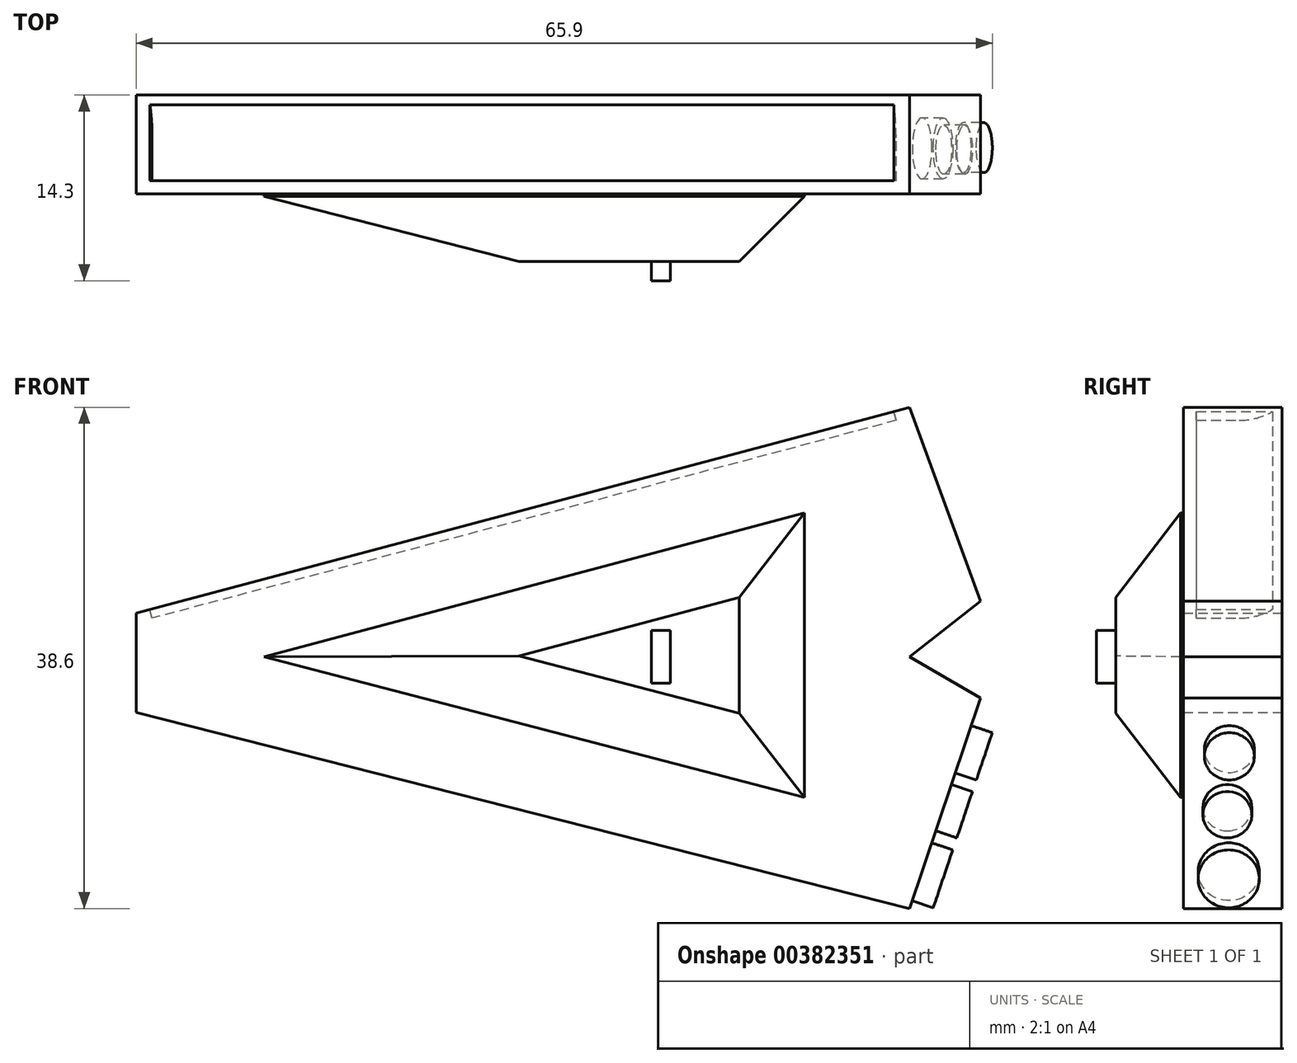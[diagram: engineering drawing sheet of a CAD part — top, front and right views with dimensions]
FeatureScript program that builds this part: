
annotation { "Feature Type Name" : "Feature", "Feature Type Description" : "" }
export const myFeature = defineFeature(function(context is Context, id is Id, definition is map)
    precondition{}
    {
        {
            var Q0;
            Q0=qCreatedBy(makeId("Front.planeOp"),FACE);
            var sketch = newSketch(context, id + "F0", { "sketchPlane" : qUnion([Q0])});
            skLineSegment(sketch, "E0", {"start": v(-59.54, 3.37) * mm, "end": v(-59.54, -4.28) * mm});
            skLineSegment(sketch, "E1", {"start": v(-59.54, -4.28) * mm, "end": v(0, -19.4) * mm});
            skLineSegment(sketch, "E2", {"start": v(0, -19.4) * mm, "end": v(5.46, -3.19) * mm});
            skLineSegment(sketch, "E3", {"start": v(5.46, -3.19) * mm, "end": v(0, 0) * mm});
            skLineSegment(sketch, "E4", {"start": v(0, 0) * mm, "end": v(5.46, 4.28) * mm});
            skLineSegment(sketch, "E5", {"start": v(5.46, 4.28) * mm, "end": v(0, 19.2) * mm});
            skLineSegment(sketch, "E6", {"start": v(0, 19.2) * mm, "end": v(-59.54, 3.37) * mm});
            skSolve(sketch);
        }
        {
            var Q0;
            Q0 = qSketchRegion(id + "F0", true);
            extrude(context, id + "F1", {"entities" : qUnion([Q0]), "depth" : 7.6 * mm});
        }
        {
            var Q0;
            Q0=makeQuery(id+"F1.opExtrude","CAP_FACE",FACE,{"disambiguationData":[OSD([sQuery(id+"F0.wireOp",EDGE,"E0"),sQuery(id+"F0.wireOp",EDGE,"E1"),sQuery(id+"F0.wireOp",EDGE,"E2"),sQuery(id+"F0.wireOp",EDGE,"E3"),sQuery(id+"F0.wireOp",EDGE,"E4"),sQuery(id+"F0.wireOp",EDGE,"E5"),sQuery(id+"F0.wireOp",EDGE,"E6")])],"isStart":false});
            var sketch = newSketch(context, id + "F2", { "sketchPlane" : qUnion([Q0])});
            skLineSegment(sketch, "E7", {"start": v(-49.7, 0) * mm, "end": v(-8.11, 11.07) * mm});
            skLineSegment(sketch, "E8", {"start": v(-8.11, 11.07) * mm, "end": v(-8.11, -10.83) * mm});
            skLineSegment(sketch, "E9", {"start": v(-8.11, -10.83) * mm, "end": v(-49.7, 0) * mm});
            skSolve(sketch);
        }
        {
            var Q0;
            Q0=makeQuery(id+"F2.imprint","IMPRINT",FACE,{"disambiguationData":[TD([[makeQuery(id+"F2.imprint","IMPRINT",EDGE,{"derivedFrom":sQuery(id+"F2.wireOp",EDGE,"E7")}),-1.0]])]});
            extrude(context, id + "F3", {"entities" : qUnion([Q0]), "operationType" : NewBodyOperationType.ADD, "depth" : 5.2 * mm});
        }
        {
            var Q0;
            Q0=makeQuery(id+"F1.opExtrude","SWEPT_FACE",FACE,{"disambiguationData":[OSD([sQuery(id+"F0.wireOp",EDGE,"E2")])]});
            var sketch = newSketch(context, id + "F4", { "sketchPlane" : qUnion([Q0])});
            skCircle(sketch, "E10", {"center": v(-4.2, -10.18) * mm, "radius": 1.88 * mm});
            skCircle(sketch, "E11", {"center": v(-4.05, -5.43) * mm, "radius": 1.92 * mm});
            skCircle(sketch, "E12", {"center": v(-4.1, -15.39) * mm, "radius": 2.35 * mm});
            skSolve(sketch);
        }
        {
            var Q0;
            Q0 = qSketchRegion(id + "F4", true);
            extrude(context, id + "F5", {"entities" : qUnion([Q0]), "operationType" : NewBodyOperationType.ADD, "depth" : 1.7 * mm});
        }
        {
            var Q0;
            Q0=makeQuery(id+"F3.opExtrude","CAP_FACE",FACE,{"disambiguationData":[OSD([sQuery(id+"F2.wireOp",EDGE,"E7"),sQuery(id+"F2.wireOp",EDGE,"E8"),sQuery(id+"F2.wireOp",EDGE,"E9")])],"isStart":false});
            chamfer(context, id + "F6", {"entities" : qUnion([Q0]), "width" : 5 * mm, "tangentPropagation" : true});
        }
        {
            var Q0;
            Q0=makeQuery(id+"F3.opExtrude","CAP_FACE",FACE,{"disambiguationData":[OSD([sQuery(id+"F2.wireOp",EDGE,"E7"),sQuery(id+"F2.wireOp",EDGE,"E8"),sQuery(id+"F2.wireOp",EDGE,"E9")])],"isStart":false});
            var sketch = newSketch(context, id + "F7", { "sketchPlane" : qUnion([Q0])});
            skLineSegment(sketch, "E13.bottom", {"start": v(-18.42, 2.02) * mm, "end": v(-19.9, 2.02) * mm});
            skLineSegment(sketch, "E13.top", {"start": v(-18.42, -2.02) * mm, "end": v(-19.9, -2.02) * mm});
            skLineSegment(sketch, "E13.left", {"start": v(-18.42, 2.02) * mm, "end": v(-18.42, -2.02) * mm});
            skLineSegment(sketch, "E13.right", {"start": v(-19.9, 2.02) * mm, "end": v(-19.9, -2.02) * mm});
            skPoint(sketch, "E13.middle", {"position": v(-19.16, 0) * mm});
            skSolve(sketch);
        }
        {
            var Q0;
            Q0=makeQuery(id+"F7.imprint","IMPRINT",FACE,{"disambiguationData":[TD([[makeQuery(id+"F7.imprint","IMPRINT",EDGE,{"derivedFrom":sQuery(id+"F7.wireOp",EDGE,"E13.bottom")}),1.0]])]});
            extrude(context, id + "F8", {"entities" : qUnion([Q0]), "operationType" : NewBodyOperationType.ADD, "depth" : 1.5 * mm});
        }
        {
            var Q0;
            Q0=makeQuery(id+"F1.opExtrude","SWEPT_FACE",FACE,{"disambiguationData":[OSD([sQuery(id+"F0.wireOp",EDGE,"E6")])]});
            var sketch = newSketch(context, id + "F9", { "sketchPlane" : qUnion([Q0])});
            skLineSegment(sketch, "E14.bottom", {"start": v(3.68, -6.6) * mm, "end": v(-55.6, -6.6) * mm});
            skLineSegment(sketch, "E14.top", {"start": v(3.68, -0.74) * mm, "end": v(-55.6, -0.74) * mm});
            skLineSegment(sketch, "E14.left", {"start": v(3.68, -6.6) * mm, "end": v(3.68, -0.74) * mm});
            skLineSegment(sketch, "E14.right", {"start": v(-55.6, -6.6) * mm, "end": v(-55.6, -0.74) * mm});
            skSolve(sketch);
        }
        {
            var Q0;
            Q0 = qSketchRegion(id + "F9", true);
            extrude(context, id + "F10", {"entities" : qUnion([Q0]), "operationType" : NewBodyOperationType.REMOVE, "oppositeDirection" : true, "depth" : 0.7 * mm});
        }
        {
            var Q0;
            Q0=makeQuery(id+"F10.boolean.opBoolean","COPY",EDGE,{"derivedFrom":makeQuery(id+"F10.opExtrude","CAP_EDGE",EDGE,{"disambiguationData":[OSD([sQuery(id+"F9.wireOp",EDGE,"E14.top")])],"isStart":false})});
            var Q1;
            Q1=makeQuery(id+"F10.boolean.opBoolean","COPY",EDGE,{"derivedFrom":makeQuery(id+"F10.opExtrude","CAP_EDGE",EDGE,{"disambiguationData":[OSD([sQuery(id+"F9.wireOp",EDGE,"E14.bottom")])],"isStart":true})});
            fillet(context, id + "F11", {"entities" : qUnion([Q0, Q1]), "radius" : 5 * mm, "tangentPropagation" : true, "allowEdgeOverflow" : false});
        }
    });
